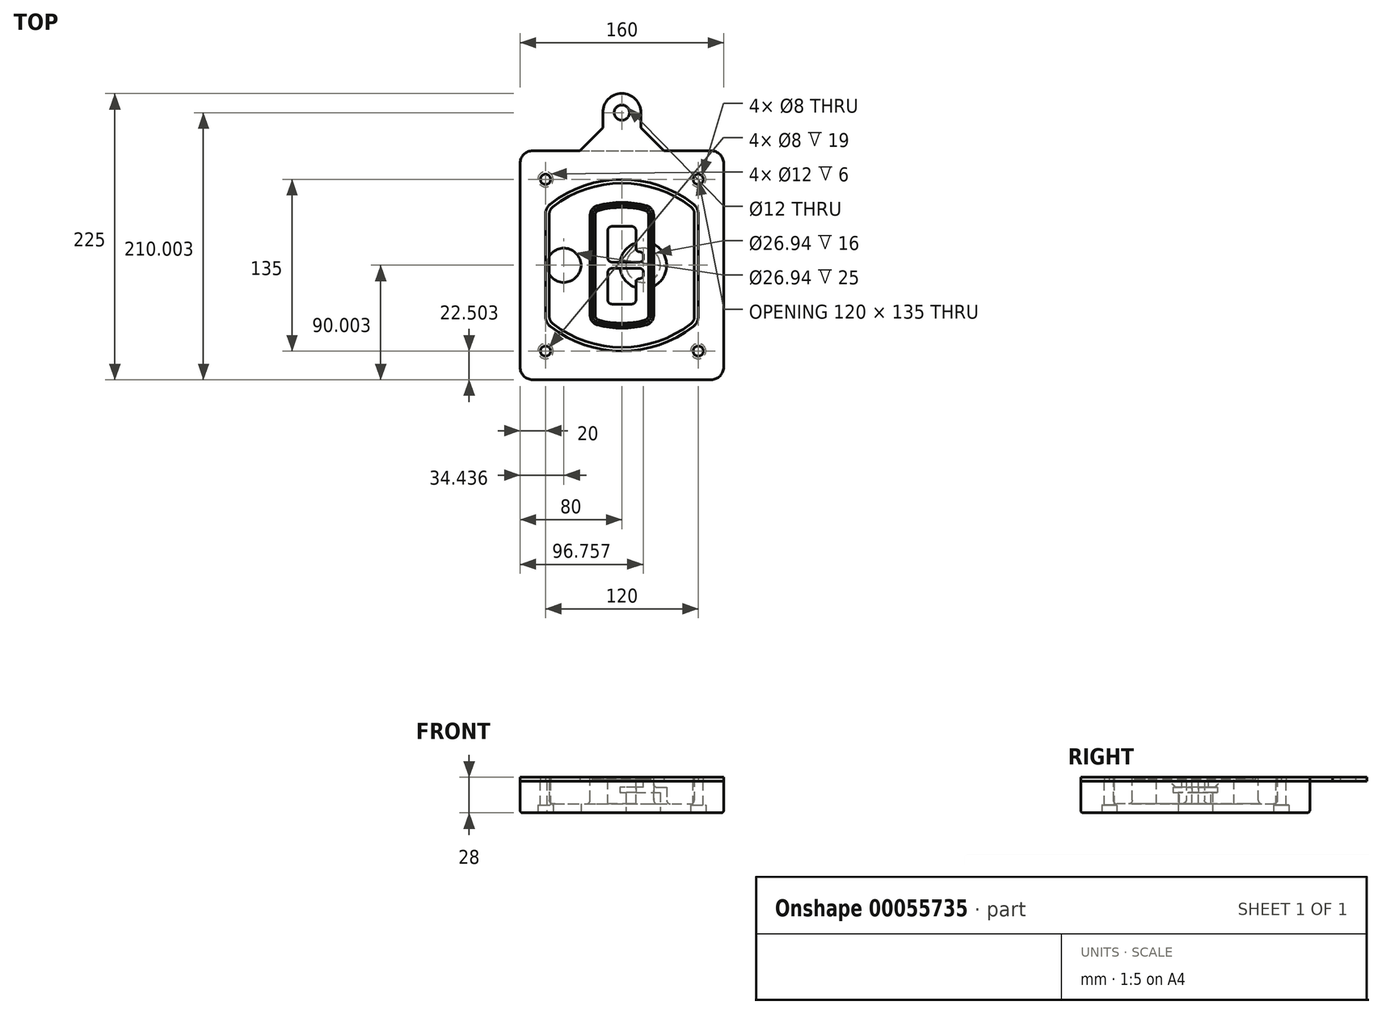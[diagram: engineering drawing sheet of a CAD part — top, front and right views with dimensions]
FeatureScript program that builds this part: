
annotation { "Feature Type Name" : "Feature", "Feature Type Description" : "" }
export const myFeature = defineFeature(function(context is Context, id is Id, definition is map)
    precondition{}
    {
        {
            var Q0;
            Q0=qCreatedBy(makeId("Top.planeOp"),FACE);
            var sketch = newSketch(context, id + "F0", { "sketchPlane" : qUnion([Q0])});
            skPoint(sketch, "E0.rect.middle", {"position": v(0, 0) * mm});
            skLineSegment(sketch, "E1.bottom", {"start": v(24.05, 28.38) * mm, "end": v(164.05, 28.38) * mm});
            skLineSegment(sketch, "E1.top", {"start": v(24.05, 208.38) * mm, "end": v(164.05, 208.38) * mm});
            skLineSegment(sketch, "E1.left", {"start": v(14.05, 38.38) * mm, "end": v(14.05, 198.38) * mm});
            skLineSegment(sketch, "E1.right", {"start": v(174.05, 38.38) * mm, "end": v(174.05, 198.38) * mm});
            skLineSegment(sketch, "E2", {"start": v(14.05, 208.38) * mm, "end": v(174.05, 28.38) * mm, "construction": true});
            skLineSegment(sketch, "E3", {"start": v(174.05, 208.38) * mm, "end": v(14.05, 28.38) * mm, "construction": true});
            skCircle(sketch, "E4", {"center": v(34.05, 185.88) * mm, "radius": 4 * mm});
            skCircle(sketch, "E5", {"center": v(154.05, 185.88) * mm, "radius": 4 * mm});
            skCircle(sketch, "E6", {"center": v(154.05, 50.88) * mm, "radius": 4 * mm});
            skCircle(sketch, "E7", {"center": v(34.05, 50.88) * mm, "radius": 4 * mm});
            skLineSegment(sketch, "E8", {"start": v(34.05, 185.88) * mm, "end": v(154.05, 185.88) * mm, "construction": true});
            skLineSegment(sketch, "E9", {"start": v(154.05, 185.88) * mm, "end": v(154.05, 50.88) * mm, "construction": true});
            skLineSegment(sketch, "E10", {"start": v(154.05, 50.88) * mm, "end": v(34.05, 50.88) * mm, "construction": true});
            skLineSegment(sketch, "E11", {"start": v(34.05, 50.88) * mm, "end": v(34.05, 185.88) * mm, "construction": true});
            skLineSegment(sketch, "E12", {"start": v(34.05, 158.68) * mm, "end": v(34.05, 78.09) * mm});
            skLineSegment(sketch, "E13", {"start": v(154.05, 158.68) * mm, "end": v(154.05, 78.09) * mm});
            skArc(sketch, "E14", {"start": v(150.2, 166.56) * mm, "mid": v(94.05, 185.88) * mm, "end": v(37.9, 166.56) * mm});
            skArc(sketch, "E15", {"start": v(37.9, 70.2) * mm, "mid": v(94.05, 50.88) * mm, "end": v(150.2, 70.2) * mm});
            skLineSegment(sketch, "E16", {"start": v(34.05, 118.38) * mm, "end": v(154.05, 118.38) * mm, "construction": true});
            skPoint(sketch, "E17.visualSharp", {"position": v(34.05, 73.38) * mm});
            skArc(sketch, "E17.filletArc", {"start": v(34.05, 78.09) * mm, "mid": v(35.06, 73.7) * mm, "end": v(37.9, 70.2) * mm});
            skPoint(sketch, "E18.visualSharp", {"position": v(34.05, 163.38) * mm});
            skArc(sketch, "E18.filletArc", {"start": v(37.9, 166.56) * mm, "mid": v(35.06, 163.06) * mm, "end": v(34.05, 158.68) * mm});
            skPoint(sketch, "E19.visualSharp", {"position": v(154.05, 163.38) * mm});
            skArc(sketch, "E19.filletArc", {"start": v(154.05, 158.68) * mm, "mid": v(153.04, 163.06) * mm, "end": v(150.2, 166.56) * mm});
            skPoint(sketch, "E20.visualSharp", {"position": v(154.05, 73.38) * mm});
            skArc(sketch, "E20.filletArc", {"start": v(150.2, 70.2) * mm, "mid": v(153.04, 73.7) * mm, "end": v(154.05, 78.09) * mm});
            skPoint(sketch, "E21.visualSharp", {"position": v(14.05, 208.38) * mm});
            skArc(sketch, "E21.filletArc", {"start": v(24.05, 208.38) * mm, "mid": v(16.98, 205.45) * mm, "end": v(14.05, 198.38) * mm});
            skPoint(sketch, "E22.visualSharp", {"position": v(174.05, 208.38) * mm});
            skArc(sketch, "E22.filletArc", {"start": v(174.05, 198.38) * mm, "mid": v(171.12, 205.45) * mm, "end": v(164.05, 208.38) * mm});
            skPoint(sketch, "E23.visualSharp", {"position": v(174.05, 28.38) * mm});
            skArc(sketch, "E23.filletArc", {"start": v(164.05, 28.38) * mm, "mid": v(171.12, 31.31) * mm, "end": v(174.05, 38.38) * mm});
            skPoint(sketch, "E24.visualSharp", {"position": v(14.05, 28.38) * mm});
            skArc(sketch, "E24.filletArc", {"start": v(14.05, 38.38) * mm, "mid": v(16.98, 31.31) * mm, "end": v(24.05, 28.38) * mm});
            skArc(sketch, "E25.0", {"start": v(151.05, 158.68) * mm, "mid": v(150.34, 161.75) * mm, "end": v(148.36, 164.2) * mm});
            skLineSegment(sketch, "E25.1", {"start": v(151.05, 158.68) * mm, "end": v(151.05, 78.09) * mm});
            skArc(sketch, "E25.2", {"start": v(148.36, 72.57) * mm, "mid": v(150.34, 75.02) * mm, "end": v(151.05, 78.09) * mm});
            skArc(sketch, "E25.3", {"start": v(39.74, 72.57) * mm, "mid": v(94.05, 53.88) * mm, "end": v(148.36, 72.57) * mm});
            skArc(sketch, "E25.4", {"start": v(37.05, 78.09) * mm, "mid": v(37.76, 75.02) * mm, "end": v(39.74, 72.57) * mm});
            skArc(sketch, "E25.5", {"start": v(148.36, 164.2) * mm, "mid": v(94.05, 182.88) * mm, "end": v(39.74, 164.2) * mm});
            skLineSegment(sketch, "E25.6", {"start": v(37.05, 158.68) * mm, "end": v(37.05, 78.09) * mm});
            skArc(sketch, "E25.7", {"start": v(39.74, 164.2) * mm, "mid": v(37.76, 161.75) * mm, "end": v(37.05, 158.68) * mm});
            skArc(sketch, "E26.0", {"start": v(35.43, 169.71) * mm, "mid": v(31.47, 164.82) * mm, "end": v(30.05, 158.68) * mm});
            skArc(sketch, "E26.1", {"start": v(152.67, 169.71) * mm, "mid": v(94.05, 189.88) * mm, "end": v(35.43, 169.71) * mm});
            skArc(sketch, "E26.2", {"start": v(158.05, 158.68) * mm, "mid": v(156.63, 164.82) * mm, "end": v(152.67, 169.71) * mm});
            skLineSegment(sketch, "E26.3", {"start": v(158.05, 158.68) * mm, "end": v(158.05, 78.09) * mm});
            skArc(sketch, "E26.4", {"start": v(152.67, 67.05) * mm, "mid": v(156.63, 71.95) * mm, "end": v(158.05, 78.09) * mm});
            skLineSegment(sketch, "E26.5", {"start": v(30.05, 158.68) * mm, "end": v(30.05, 78.09) * mm});
            skArc(sketch, "E26.6", {"start": v(35.43, 67.05) * mm, "mid": v(94.05, 46.88) * mm, "end": v(152.67, 67.05) * mm});
            skArc(sketch, "E26.7", {"start": v(30.05, 78.09) * mm, "mid": v(31.47, 71.95) * mm, "end": v(35.43, 67.05) * mm});
            skSolve(sketch);
        }
        {
            var Q0;
            Q0=makeQuery(id+"F0.imprint","IMPRINT",FACE,{"disambiguationData":[TD([[makeQuery(id+"F0.imprint","IMPRINT",EDGE,{"derivedFrom":sQuery(id+"F0.wireOp",EDGE,"E1.bottom")}),1.0]])]});
            var Q1;
            Q1=makeQuery(id+"F0.imprint","IMPRINT",FACE,{"disambiguationData":[TD([[makeQuery(id+"F0.imprint","IMPRINT",EDGE,{"derivedFrom":sQuery(id+"F0.wireOp",EDGE,"E12")}),1.0]])]});
            var Q2;
            Q2=makeQuery(id+"F0.imprint","IMPRINT",FACE,{"disambiguationData":[TD([[makeQuery(id+"F0.imprint","IMPRINT",EDGE,{"derivedFrom":sQuery(id+"F0.wireOp",EDGE,"E25.0")}),1.0]])]});
            var Q3;
            Q3=makeQuery(id+"F0.imprint","IMPRINT",FACE,{"disambiguationData":[TD([[makeQuery(id+"F0.imprint","IMPRINT",EDGE,{"derivedFrom":sQuery(id+"F0.wireOp",EDGE,"E12")}),-1.0]])]});
            extrude(context, id + "F1", {"entities" : qUnion([Q0, Q1, Q2, Q3]), "oppositeDirection" : true, "depth" : 25 * mm});
        }
        {
            var Q0;
            Q0=makeQuery(id+"F0.imprint","IMPRINT",FACE,{"disambiguationData":[TD([[makeQuery(id+"F0.imprint","IMPRINT",EDGE,{"derivedFrom":sQuery(id+"F0.wireOp",EDGE,"E12")}),1.0]])]});
            extrude(context, id + "F2", {"entities" : qUnion([Q0]), "operationType" : NewBodyOperationType.ADD, "depth" : 3 * mm});
        }
        {
            var Q0;
            Q0=makeQuery(id+"F0.imprint","IMPRINT",FACE,{"disambiguationData":[TD([[makeQuery(id+"F0.imprint","IMPRINT",EDGE,{"derivedFrom":sQuery(id+"F0.wireOp",EDGE,"E25.0")}),1.0]])]});
            extrude(context, id + "F3", {"entities" : qUnion([Q0]), "operationType" : NewBodyOperationType.REMOVE, "oppositeDirection" : true, "depth" : 18 * mm});
        }
        {
            var Q0;
            Q0=makeQuery(id+"F2.opExtrude","CAP_FACE",FACE,{"disambiguationData":[OSD([sQuery(id+"F0.wireOp",EDGE,"E12"),sQuery(id+"F0.wireOp",EDGE,"E13"),sQuery(id+"F0.wireOp",EDGE,"E14"),sQuery(id+"F0.wireOp",EDGE,"E15"),sQuery(id+"F0.wireOp",EDGE,"E17.filletArc"),sQuery(id+"F0.wireOp",EDGE,"E18.filletArc"),sQuery(id+"F0.wireOp",EDGE,"E19.filletArc"),sQuery(id+"F0.wireOp",EDGE,"E20.filletArc"),sQuery(id+"F0.wireOp",EDGE,"E25.0"),sQuery(id+"F0.wireOp",EDGE,"E25.1"),sQuery(id+"F0.wireOp",EDGE,"E25.2"),sQuery(id+"F0.wireOp",EDGE,"E25.3"),sQuery(id+"F0.wireOp",EDGE,"E25.4"),sQuery(id+"F0.wireOp",EDGE,"E25.5"),sQuery(id+"F0.wireOp",EDGE,"E25.6"),sQuery(id+"F0.wireOp",EDGE,"E25.7")])],"isStart":false});
            var sketch = newSketch(context, id + "F4", { "sketchPlane" : qUnion([Q0])});
            skArc(sketch, "E27.0", {"start": v(74.97, 71.41) * mm, "mid": v(94.05, 68.88) * mm, "end": v(113.13, 71.41) * mm});
            skArc(sketch, "E28.0", {"start": v(113.13, 165.35) * mm, "mid": v(94.05, 167.88) * mm, "end": v(74.97, 165.35) * mm});
            skLineSegment(sketch, "E29", {"start": v(69.05, 157.63) * mm, "end": v(69.05, 79.14) * mm});
            skLineSegment(sketch, "E30", {"start": v(119.05, 157.63) * mm, "end": v(119.05, 79.14) * mm});
            skLineSegment(sketch, "E31", {"start": v(69.05, 163.48) * mm, "end": v(119.05, 163.48) * mm, "construction": true});
            skLineSegment(sketch, "E32", {"start": v(69.05, 73.28) * mm, "end": v(119.05, 73.28) * mm, "construction": true});
            skPoint(sketch, "E33.visualSharp", {"position": v(69.05, 163.48) * mm});
            skArc(sketch, "E33.filletArc", {"start": v(74.97, 165.35) * mm, "mid": v(70.7, 162.5) * mm, "end": v(69.05, 157.63) * mm});
            skPoint(sketch, "E34.visualSharp", {"position": v(119.05, 163.48) * mm});
            skArc(sketch, "E34.filletArc", {"start": v(119.05, 157.63) * mm, "mid": v(117.4, 162.5) * mm, "end": v(113.13, 165.35) * mm});
            skPoint(sketch, "E35.visualSharp", {"position": v(119.05, 73.28) * mm});
            skArc(sketch, "E35.filletArc", {"start": v(113.13, 71.41) * mm, "mid": v(117.4, 74.27) * mm, "end": v(119.05, 79.14) * mm});
            skPoint(sketch, "E36.visualSharp", {"position": v(69.05, 73.28) * mm});
            skArc(sketch, "E36.filletArc", {"start": v(69.05, 79.14) * mm, "mid": v(70.7, 74.27) * mm, "end": v(74.97, 71.41) * mm});
            skArc(sketch, "E37.0", {"start": v(148.36, 164.2) * mm, "mid": v(94.05, 182.88) * mm, "end": v(39.74, 164.2) * mm});
            skArc(sketch, "E37.1", {"start": v(39.74, 164.2) * mm, "mid": v(37.76, 161.75) * mm, "end": v(37.05, 158.68) * mm});
            skLineSegment(sketch, "E37.2", {"start": v(37.05, 158.68) * mm, "end": v(37.05, 78.09) * mm});
            skArc(sketch, "E37.3", {"start": v(37.05, 78.09) * mm, "mid": v(37.76, 75.02) * mm, "end": v(39.74, 72.57) * mm});
            skArc(sketch, "E37.4", {"start": v(39.74, 72.57) * mm, "mid": v(94.05, 53.88) * mm, "end": v(148.36, 72.57) * mm});
            skArc(sketch, "E37.5", {"start": v(148.36, 72.57) * mm, "mid": v(150.34, 75.02) * mm, "end": v(151.05, 78.09) * mm});
            skLineSegment(sketch, "E37.6", {"start": v(151.05, 158.68) * mm, "end": v(151.05, 78.09) * mm});
            skArc(sketch, "E37.7", {"start": v(151.05, 158.68) * mm, "mid": v(150.34, 161.75) * mm, "end": v(148.36, 164.2) * mm});
            skLineSegment(sketch, "E38.0", {"start": v(117.05, 157.63) * mm, "end": v(117.05, 79.14) * mm});
            skArc(sketch, "E38.1", {"start": v(112.61, 73.34) * mm, "mid": v(115.81, 75.49) * mm, "end": v(117.05, 79.14) * mm});
            skArc(sketch, "E38.2", {"start": v(75.49, 73.34) * mm, "mid": v(94.05, 70.88) * mm, "end": v(112.61, 73.34) * mm});
            skArc(sketch, "E38.3", {"start": v(71.05, 79.14) * mm, "mid": v(72.29, 75.49) * mm, "end": v(75.49, 73.34) * mm});
            skLineSegment(sketch, "E38.4", {"start": v(71.05, 157.63) * mm, "end": v(71.05, 79.14) * mm});
            skArc(sketch, "E38.5", {"start": v(117.05, 157.63) * mm, "mid": v(115.81, 161.28) * mm, "end": v(112.61, 163.42) * mm});
            skArc(sketch, "E38.6", {"start": v(75.49, 163.42) * mm, "mid": v(72.29, 161.28) * mm, "end": v(71.05, 157.63) * mm});
            skArc(sketch, "E38.7", {"start": v(112.61, 163.42) * mm, "mid": v(94.05, 165.88) * mm, "end": v(75.49, 163.42) * mm});
            skArc(sketch, "E39.0", {"start": v(115.05, 157.63) * mm, "mid": v(114.23, 160.06) * mm, "end": v(112.1, 161.5) * mm});
            skLineSegment(sketch, "E39.1", {"start": v(115.05, 157.63) * mm, "end": v(115.05, 79.14) * mm});
            skArc(sketch, "E39.2", {"start": v(112.1, 75.27) * mm, "mid": v(114.23, 76.7) * mm, "end": v(115.05, 79.14) * mm});
            skArc(sketch, "E39.3", {"start": v(76, 75.27) * mm, "mid": v(94.05, 72.88) * mm, "end": v(112.1, 75.27) * mm});
            skArc(sketch, "E39.4", {"start": v(73.05, 79.14) * mm, "mid": v(73.87, 76.7) * mm, "end": v(76, 75.27) * mm});
            skArc(sketch, "E39.5", {"start": v(112.1, 161.5) * mm, "mid": v(94.05, 163.88) * mm, "end": v(76, 161.5) * mm});
            skLineSegment(sketch, "E39.6", {"start": v(73.05, 157.63) * mm, "end": v(73.05, 79.14) * mm});
            skArc(sketch, "E39.7", {"start": v(76, 161.5) * mm, "mid": v(73.87, 160.06) * mm, "end": v(73.05, 157.63) * mm});
            skLineSegment(sketch, "E40", {"start": v(69.05, 118.38) * mm, "end": v(119.05, 118.38) * mm, "construction": true});
            skLineSegment(sketch, "E41", {"start": v(83.05, 123.88) * mm, "end": v(83.05, 145.88) * mm});
            skLineSegment(sketch, "E42", {"start": v(86.05, 148.88) * mm, "end": v(102.05, 148.88) * mm});
            skLineSegment(sketch, "E43", {"start": v(105.05, 145.88) * mm, "end": v(105.05, 131.88) * mm});
            skLineSegment(sketch, "E44", {"start": v(108.05, 128.88) * mm, "end": v(108.05, 128.88) * mm});
            skLineSegment(sketch, "E45", {"start": v(111.05, 125.88) * mm, "end": v(111.05, 123.88) * mm});
            skLineSegment(sketch, "E46", {"start": v(108.05, 120.88) * mm, "end": v(86.05, 120.88) * mm});
            skPoint(sketch, "E47.visualSharp", {"position": v(83.05, 148.88) * mm});
            skArc(sketch, "E47.filletArc", {"start": v(86.05, 148.88) * mm, "mid": v(83.93, 148) * mm, "end": v(83.05, 145.88) * mm});
            skPoint(sketch, "E48.visualSharp", {"position": v(105.05, 148.88) * mm});
            skArc(sketch, "E48.filletArc", {"start": v(105.05, 145.88) * mm, "mid": v(104.17, 148) * mm, "end": v(102.05, 148.88) * mm});
            skPoint(sketch, "E49.visualSharp", {"position": v(105.05, 128.88) * mm});
            skArc(sketch, "E49.filletArc", {"start": v(105.05, 131.88) * mm, "mid": v(105.93, 129.76) * mm, "end": v(108.05, 128.88) * mm});
            skPoint(sketch, "E50.visualSharp", {"position": v(111.05, 128.88) * mm});
            skArc(sketch, "E50.filletArc", {"start": v(111.05, 125.88) * mm, "mid": v(110.17, 128) * mm, "end": v(108.05, 128.88) * mm});
            skPoint(sketch, "E51.visualSharp", {"position": v(111.05, 120.88) * mm});
            skArc(sketch, "E51.filletArc", {"start": v(108.05, 120.88) * mm, "mid": v(110.17, 121.76) * mm, "end": v(111.05, 123.88) * mm});
            skPoint(sketch, "E52.visualSharp", {"position": v(83.05, 120.88) * mm});
            skArc(sketch, "E52.filletArc", {"start": v(83.05, 123.88) * mm, "mid": v(83.93, 121.76) * mm, "end": v(86.05, 120.88) * mm});
            skLineSegment(sketch, "E53.0.MirrorCS", {"start": v(108.05, 115.88) * mm, "end": v(86.05, 115.88) * mm});
            skArc(sketch, "E54.0.MirrorCS", {"start": v(83.05, 112.88) * mm, "mid": v(83.93, 115) * mm, "end": v(86.05, 115.88) * mm});
            skLineSegment(sketch, "E55.0.MirrorCS", {"start": v(83.05, 112.88) * mm, "end": v(83.05, 90.88) * mm});
            skArc(sketch, "E56.0.MirrorCS", {"start": v(86.05, 87.88) * mm, "mid": v(83.93, 88.76) * mm, "end": v(83.05, 90.88) * mm});
            skLineSegment(sketch, "E57.0.MirrorCS", {"start": v(86.05, 87.88) * mm, "end": v(102.05, 87.88) * mm});
            skArc(sketch, "E58.0.MirrorCS", {"start": v(105.05, 90.88) * mm, "mid": v(104.17, 88.76) * mm, "end": v(102.05, 87.88) * mm});
            skLineSegment(sketch, "E59.0.MirrorCS", {"start": v(105.05, 90.88) * mm, "end": v(105.05, 104.88) * mm});
            skArc(sketch, "E60.0.MirrorCS", {"start": v(105.05, 104.88) * mm, "mid": v(105.93, 107) * mm, "end": v(108.05, 107.88) * mm});
            skArc(sketch, "E61.0.MirrorCS", {"start": v(111.05, 110.88) * mm, "mid": v(110.17, 108.76) * mm, "end": v(108.05, 107.88) * mm});
            skLineSegment(sketch, "E62.0.MirrorCS", {"start": v(111.05, 110.88) * mm, "end": v(111.05, 112.88) * mm});
            skArc(sketch, "E63.0.MirrorCS", {"start": v(108.05, 115.88) * mm, "mid": v(110.17, 115) * mm, "end": v(111.05, 112.88) * mm});
            skSolve(sketch);
        }
        {
            var Q0;
            Q0=makeQuery(id+"F4.imprint","IMPRINT",FACE,{"disambiguationData":[TD([[makeQuery(id+"F4.imprint","IMPRINT",EDGE,{"derivedFrom":sQuery(id+"F4.wireOp",EDGE,"E27.0")}),1.0]])]});
            var Q1;
            Q1=makeQuery(id+"F4.imprint","IMPRINT",FACE,{"disambiguationData":[TD([[makeQuery(id+"F4.imprint","IMPRINT",EDGE,{"derivedFrom":sQuery(id+"F4.wireOp",EDGE,"E38.0")}),-1.0]])]});
            var Q2;
            Q2=makeQuery(id+"F4.imprint","IMPRINT",FACE,{"disambiguationData":[TD([[makeQuery(id+"F4.imprint","IMPRINT",EDGE,{"derivedFrom":sQuery(id+"F4.wireOp",EDGE,"E39.0")}),1.0]])]});
            extrude(context, id + "F5", {"entities" : qUnion([Q0, Q1, Q2]), "operationType" : NewBodyOperationType.ADD, "endBound" : BoundingType.UP_TO_NEXT, "oppositeDirection" : true, "depth" : 25 * mm});
        }
        {
            var Q0;
            Q0=makeQuery(id+"F4.imprint","IMPRINT",FACE,{"disambiguationData":[TD([[makeQuery(id+"F4.imprint","IMPRINT",EDGE,{"derivedFrom":sQuery(id+"F4.wireOp",EDGE,"E38.0")}),-1.0]])]});
            extrude(context, id + "F6", {"entities" : qUnion([Q0]), "operationType" : NewBodyOperationType.REMOVE, "oppositeDirection" : true, "depth" : 2 * mm});
        }
        {
            var Q0;
            Q0=makeQuery(id+"F1.opExtrude","CAP_FACE",FACE,{"disambiguationData":[OSD([sQuery(id+"F0.wireOp",EDGE,"E1.bottom"),sQuery(id+"F0.wireOp",EDGE,"E1.top"),sQuery(id+"F0.wireOp",EDGE,"E1.left"),sQuery(id+"F0.wireOp",EDGE,"E1.right"),sQuery(id+"F0.wireOp",EDGE,"E4"),sQuery(id+"F0.wireOp",EDGE,"E5"),sQuery(id+"F0.wireOp",EDGE,"E6"),sQuery(id+"F0.wireOp",EDGE,"E7"),sQuery(id+"F0.wireOp",EDGE,"E21.filletArc"),sQuery(id+"F0.wireOp",EDGE,"E22.filletArc"),sQuery(id+"F0.wireOp",EDGE,"E23.filletArc"),sQuery(id+"F0.wireOp",EDGE,"E24.filletArc")])],"isStart":false});
            var sketch = newSketch(context, id + "F7", { "sketchPlane" : qUnion([Q0])});
            skCircle(sketch, "E64", {"center": v(110.8, -118.38) * mm, "radius": 13.47 * mm});
            skCircle(sketch, "E65", {"center": v(48.49, -118.38) * mm, "radius": 13.47 * mm});
            skLineSegment(sketch, "E66", {"start": v(174.05, -118.38) * mm, "end": v(14.05, -118.38) * mm});
            skCircle(sketch, "E67", {"center": v(110.8, -118.38) * mm, "radius": 18.47 * mm});
            skCircle(sketch, "E68", {"center": v(154.05, -185.88) * mm, "radius": 6 * mm});
            skCircle(sketch, "E69", {"center": v(34.05, -185.88) * mm, "radius": 6 * mm});
            skCircle(sketch, "E70", {"center": v(34.05, -50.88) * mm, "radius": 6 * mm});
            skCircle(sketch, "E71", {"center": v(154.05, -50.88) * mm, "radius": 6 * mm});
            skSolve(sketch);
        }
        {
            var Q0;
            {var subQ1=sQuery(id+"F7.wireOp",EDGE,"E66");var subQ4=sQuery(id+"F7.wireOp",EDGE,"E64");var subQ6=makeQuery(id+"F7.imprint","INTERSECT",VERTEX,{"disambiguationData":[OD(0.0)],"derivedFrom":[subQ4,subQ1]});Q0=makeQuery(id+"F7.imprint","IMPRINT",FACE,{"disambiguationData":[TD([[makeQuery(id+"F7.imprint","IMPRINT",EDGE,{"disambiguationData":[TD([[subQ6,-1.0]])],"derivedFrom":subQ4}),-1.0]])]});}
            var Q1;
            {var subQ0=sQuery(id+"F7.wireOp",EDGE,"E66");var subQ1=sQuery(id+"F7.wireOp",EDGE,"E64");var subQ3=makeQuery(id+"F7.imprint","INTERSECT",VERTEX,{"disambiguationData":[OD(0.0)],"derivedFrom":[subQ1,subQ0]});Q1=makeQuery(id+"F7.imprint","IMPRINT",FACE,{"disambiguationData":[TD([[makeQuery(id+"F7.imprint","IMPRINT",EDGE,{"disambiguationData":[TD([[subQ3,-1.0]])],"derivedFrom":subQ1}),1.0]])]});}
            var Q2;
            {var subQ0=sQuery(id+"F7.wireOp",EDGE,"E66");var subQ1=sQuery(id+"F7.wireOp",EDGE,"E64");var subQ3=makeQuery(id+"F7.imprint","INTERSECT",VERTEX,{"disambiguationData":[OD(0.0)],"derivedFrom":[subQ1,subQ0]});Q2=makeQuery(id+"F7.imprint","IMPRINT",FACE,{"disambiguationData":[TD([[makeQuery(id+"F7.imprint","IMPRINT",EDGE,{"disambiguationData":[TD([[subQ3,1.0]])],"derivedFrom":subQ1}),1.0]])]});}
            var Q3;
            {var subQ1=sQuery(id+"F7.wireOp",EDGE,"E66");var subQ4=sQuery(id+"F7.wireOp",EDGE,"E64");var subQ6=makeQuery(id+"F7.imprint","INTERSECT",VERTEX,{"disambiguationData":[OD(0.0)],"derivedFrom":[subQ4,subQ1]});Q3=makeQuery(id+"F7.imprint","IMPRINT",FACE,{"disambiguationData":[TD([[makeQuery(id+"F7.imprint","IMPRINT",EDGE,{"disambiguationData":[TD([[subQ6,1.0]])],"derivedFrom":subQ4}),-1.0]])]});}
            extrude(context, id + "F8", {"entities" : qUnion([Q0, Q1, Q2, Q3]), "operationType" : NewBodyOperationType.ADD, "oppositeDirection" : true, "depth" : 20 * mm});
        }
        {
            var Q0;
            {var subQ0=sQuery(id+"F7.wireOp",EDGE,"E66");var subQ1=sQuery(id+"F7.wireOp",EDGE,"E64");var subQ3=makeQuery(id+"F7.imprint","INTERSECT",VERTEX,{"disambiguationData":[OD(0.0)],"derivedFrom":[subQ1,subQ0]});Q0=makeQuery(id+"F7.imprint","IMPRINT",FACE,{"disambiguationData":[TD([[makeQuery(id+"F7.imprint","IMPRINT",EDGE,{"disambiguationData":[TD([[subQ3,-1.0]])],"derivedFrom":subQ1}),1.0]])]});}
            var Q1;
            {var subQ0=sQuery(id+"F7.wireOp",EDGE,"E66");var subQ1=sQuery(id+"F7.wireOp",EDGE,"E64");var subQ3=makeQuery(id+"F7.imprint","INTERSECT",VERTEX,{"disambiguationData":[OD(0.0)],"derivedFrom":[subQ1,subQ0]});Q1=makeQuery(id+"F7.imprint","IMPRINT",FACE,{"disambiguationData":[TD([[makeQuery(id+"F7.imprint","IMPRINT",EDGE,{"disambiguationData":[TD([[subQ3,1.0]])],"derivedFrom":subQ1}),1.0]])]});}
            extrude(context, id + "F9", {"entities" : qUnion([Q0, Q1]), "operationType" : NewBodyOperationType.REMOVE, "oppositeDirection" : true, "depth" : 16 * mm});
        }
        {
            var Q0;
            {var subQ0=sQuery(id+"F7.wireOp",EDGE,"E66");var subQ1=sQuery(id+"F7.wireOp",EDGE,"E65");var subQ3=makeQuery(id+"F7.imprint","INTERSECT",VERTEX,{"disambiguationData":[OD(0.0)],"derivedFrom":[subQ1,subQ0]});Q0=makeQuery(id+"F7.imprint","IMPRINT",FACE,{"disambiguationData":[TD([[makeQuery(id+"F7.imprint","IMPRINT",EDGE,{"disambiguationData":[TD([[subQ3,-1.0]])],"derivedFrom":subQ1}),1.0]])]});}
            var Q1;
            {var subQ0=sQuery(id+"F7.wireOp",EDGE,"E66");var subQ1=sQuery(id+"F7.wireOp",EDGE,"E65");var subQ3=makeQuery(id+"F7.imprint","INTERSECT",VERTEX,{"disambiguationData":[OD(0.0)],"derivedFrom":[subQ1,subQ0]});Q1=makeQuery(id+"F7.imprint","IMPRINT",FACE,{"disambiguationData":[TD([[makeQuery(id+"F7.imprint","IMPRINT",EDGE,{"disambiguationData":[TD([[subQ3,1.0]])],"derivedFrom":subQ1}),1.0]])]});}
            extrude(context, id + "F10", {"entities" : qUnion([Q0, Q1]), "operationType" : NewBodyOperationType.REMOVE, "oppositeDirection" : true, "depth" : 25 * mm});
        }
        {
            var Q0;
            Q0=makeQuery(id+"F7.imprint","IMPRINT",FACE,{"disambiguationData":[TD([[makeQuery(id+"F7.imprint","IMPRINT",EDGE,{"derivedFrom":sQuery(id+"F7.wireOp",EDGE,"E68")}),1.0]])]});
            var Q1;
            Q1=makeQuery(id+"F7.imprint","IMPRINT",FACE,{"disambiguationData":[TD([[makeQuery(id+"F7.imprint","IMPRINT",EDGE,{"derivedFrom":makeQuery(id+"F1.opExtrude","CAP_EDGE",EDGE,{"disambiguationData":[OSD([sQuery(id+"F0.wireOp",EDGE,"E5")])],"isStart":false})}),-1.0]])]});
            var Q2;
            Q2=makeQuery(id+"F7.imprint","IMPRINT",FACE,{"disambiguationData":[TD([[makeQuery(id+"F7.imprint","IMPRINT",EDGE,{"derivedFrom":sQuery(id+"F7.wireOp",EDGE,"E69")}),1.0]])]});
            var Q3;
            Q3=makeQuery(id+"F7.imprint","IMPRINT",FACE,{"disambiguationData":[TD([[makeQuery(id+"F7.imprint","IMPRINT",EDGE,{"derivedFrom":makeQuery(id+"F1.opExtrude","CAP_EDGE",EDGE,{"disambiguationData":[OSD([sQuery(id+"F0.wireOp",EDGE,"E4")])],"isStart":false})}),-1.0]])]});
            var Q4;
            Q4=makeQuery(id+"F7.imprint","IMPRINT",FACE,{"disambiguationData":[TD([[makeQuery(id+"F7.imprint","IMPRINT",EDGE,{"derivedFrom":sQuery(id+"F7.wireOp",EDGE,"E70")}),1.0]])]});
            var Q5;
            Q5=makeQuery(id+"F7.imprint","IMPRINT",FACE,{"disambiguationData":[TD([[makeQuery(id+"F7.imprint","IMPRINT",EDGE,{"derivedFrom":makeQuery(id+"F1.opExtrude","CAP_EDGE",EDGE,{"disambiguationData":[OSD([sQuery(id+"F0.wireOp",EDGE,"E7")])],"isStart":false})}),-1.0]])]});
            var Q6;
            Q6=makeQuery(id+"F7.imprint","IMPRINT",FACE,{"disambiguationData":[TD([[makeQuery(id+"F7.imprint","IMPRINT",EDGE,{"derivedFrom":sQuery(id+"F7.wireOp",EDGE,"E71")}),1.0]])]});
            var Q7;
            Q7=makeQuery(id+"F7.imprint","IMPRINT",FACE,{"disambiguationData":[TD([[makeQuery(id+"F7.imprint","IMPRINT",EDGE,{"derivedFrom":makeQuery(id+"F1.opExtrude","CAP_EDGE",EDGE,{"disambiguationData":[OSD([sQuery(id+"F0.wireOp",EDGE,"E6")])],"isStart":false})}),-1.0]])]});
            extrude(context, id + "F11", {"entities" : qUnion([Q0, Q1, Q2, Q3, Q4, Q5, Q6, Q7]), "operationType" : NewBodyOperationType.REMOVE, "oppositeDirection" : true, "depth" : 6 * mm});
        }
        {
            var Q0;
            Q0=makeQuery(id+"F9.boolean.opBoolean","COPY",FACE,{"derivedFrom":makeQuery(id+"F9.opExtrude","CAP_FACE",FACE,{"disambiguationData":[OSD([sQuery(id+"F7.wireOp",EDGE,"E64")])],"isStart":false})});
            var sketch = newSketch(context, id + "F12", { "sketchPlane" : qUnion([Q0])});
            skArc(sketch, "E72.0", {"start": v(105.05, -100.83) * mm, "mid": v(96.62, -106.56) * mm, "end": v(92.5, -115.88) * mm});
            skArc(sketch, "E72.1", {"start": v(92.5, -120.88) * mm, "mid": v(96.62, -130.2) * mm, "end": v(105.05, -135.93) * mm});
            skLineSegment(sketch, "E73", {"start": v(92.5, -120.88) * mm, "end": v(108.05, -120.88) * mm});
            skLineSegment(sketch, "E74.0", {"start": v(108.05, -115.88) * mm, "end": v(92.5, -115.88) * mm});
            skArc(sketch, "E74.1", {"start": v(108.05, -115.88) * mm, "mid": v(110.17, -115) * mm, "end": v(111.05, -112.88) * mm});
            skLineSegment(sketch, "E74.2", {"start": v(111.05, -110.88) * mm, "end": v(111.05, -112.88) * mm});
            skArc(sketch, "E74.3", {"start": v(111.05, -110.88) * mm, "mid": v(110.17, -108.76) * mm, "end": v(108.05, -107.88) * mm});
            skArc(sketch, "E74.4", {"start": v(105.05, -104.88) * mm, "mid": v(105.93, -107) * mm, "end": v(108.05, -107.88) * mm});
            skLineSegment(sketch, "E74.5", {"start": v(105.05, -100.83) * mm, "end": v(105.05, -104.88) * mm});
            skLineSegment(sketch, "E74.7", {"start": v(108.05, -120.88) * mm, "end": v(92.5, -120.88) * mm});
            skArc(sketch, "E74.8", {"start": v(108.05, -120.88) * mm, "mid": v(110.17, -121.76) * mm, "end": v(111.05, -123.88) * mm});
            skLineSegment(sketch, "E74.9", {"start": v(111.05, -125.88) * mm, "end": v(111.05, -123.88) * mm});
            skArc(sketch, "E74.10", {"start": v(111.05, -125.88) * mm, "mid": v(110.17, -128) * mm, "end": v(108.05, -128.88) * mm});
            skArc(sketch, "E74.11", {"start": v(105.05, -131.88) * mm, "mid": v(105.93, -129.76) * mm, "end": v(108.05, -128.88) * mm});
            skLineSegment(sketch, "E74.12", {"start": v(105.05, -135.93) * mm, "end": v(105.05, -131.88) * mm});
            skPoint(sketch, "E75.orphan", {"position": v(105.05, -145.88) * mm});
            skPoint(sketch, "E76.orphan", {"position": v(86.05, -120.88) * mm});
            skPoint(sketch, "E77.orphan", {"position": v(86.05, -115.88) * mm});
            skPoint(sketch, "E78.orphan", {"position": v(105.05, -90.88) * mm});
            skSolve(sketch);
        }
        {
            var Q0;
            {var subQ7=sQuery(id+"F12.wireOp",EDGE,"E72.0");var subQ14=sQuery(id+"F12.wireOp",EDGE,"E72.1");var subQ16=sQuery(id+"F12.wireOp",EDGE,"E74.1");var subQ18=sQuery(id+"F12.wireOp",EDGE,"E74.8");Q0=qUnion([makeQuery(id+"F12.imprint","IMPRINT",FACE,{"disambiguationData":[TD([[makeQuery(id+"F12.imprint","IMPRINT",EDGE,{"derivedFrom":subQ7}),1.0]])]}),makeQuery(id+"F12.imprint","IMPRINT",FACE,{"disambiguationData":[TD([[makeQuery(id+"F12.imprint","IMPRINT",EDGE,{"derivedFrom":subQ14}),1.0]])]}),makeQuery(id+"F12.imprint","IMPRINT",FACE,{"disambiguationData":[TD([[makeQuery(id+"F12.imprint","IMPRINT",EDGE,{"derivedFrom":subQ16}),1.0]])]}),makeQuery(id+"F12.imprint","IMPRINT",FACE,{"disambiguationData":[TD([[makeQuery(id+"F12.imprint","IMPRINT",EDGE,{"derivedFrom":subQ18}),-1.0]])]})]);}
            var Q1;
            Q1=makeQuery(id+"F5.boolean.opBoolean","SPLIT",FACE,{"disambiguationData":[TD([makeQuery(id+"F5.opExtrude","SWEPT_FACE",FACE,{"disambiguationData":[OSD([sQuery(id+"F4.wireOp",EDGE,"E41")])]})])],"derivedFrom":makeQuery(id+"F3.boolean.opBoolean","COPY",FACE,{"derivedFrom":makeQuery(id+"F3.opExtrude","CAP_FACE",FACE,{"disambiguationData":[OSD([sQuery(id+"F0.wireOp",EDGE,"E25.0"),sQuery(id+"F0.wireOp",EDGE,"E25.1"),sQuery(id+"F0.wireOp",EDGE,"E25.2"),sQuery(id+"F0.wireOp",EDGE,"E25.3"),sQuery(id+"F0.wireOp",EDGE,"E25.4"),sQuery(id+"F0.wireOp",EDGE,"E25.5"),sQuery(id+"F0.wireOp",EDGE,"E25.6"),sQuery(id+"F0.wireOp",EDGE,"E25.7")])],"isStart":false})})});
            extrude(context, id + "F13", {"entities" : qUnion([Q0]), "operationType" : NewBodyOperationType.REMOVE, "endBound" : BoundingType.UP_TO_SURFACE, "endBoundEntityFace" : qUnion([Q1]), "depth" : 25 * mm});
        }
        {
            var Q0;
            Q0=makeQuery(id+"F3.boolean.opBoolean","COPY",EDGE,{"derivedFrom":makeQuery(id+"F3.opExtrude","CAP_EDGE",EDGE,{"disambiguationData":[OSD([sQuery(id+"F0.wireOp",EDGE,"E25.6")])],"isStart":false})});
            var Q1;
            Q1=makeQuery(id+"F8.boolean.opBoolean","INTERSECT",EDGE,{"derivedFrom":[makeQuery(id+"F5.opExtrude","SWEPT_FACE",FACE,{"disambiguationData":[OSD([sQuery(id+"F4.wireOp",EDGE,"E30")])]}),makeQuery(id+"F8.opExtrude","CAP_FACE",FACE,{"disambiguationData":[OSD([sQuery(id+"F7.wireOp",EDGE,"E67")])],"isStart":false})]});
            var Q2;
            Q2=makeQuery(id+"F8.boolean.opBoolean","INTERSECT",EDGE,{"disambiguationData":[OD(1.0)],"derivedFrom":[makeQuery(id+"F5.opExtrude","SWEPT_FACE",FACE,{"disambiguationData":[OSD([sQuery(id+"F4.wireOp",EDGE,"E30")])]}),makeQuery(id+"F8.opExtrude","SWEPT_FACE",FACE,{"disambiguationData":[OSD([sQuery(id+"F7.wireOp",EDGE,"E67")])]})]});
            var Q3;
            {var subQ0=sQuery(id+"F4.wireOp",EDGE,"E30");Q3=makeQuery(id+"F8.boolean.opBoolean","SPLIT",EDGE,{"disambiguationData":[TD([makeQuery(id+"F5.opExtrude","SWEPT_FACE",FACE,{"disambiguationData":[OSD([sQuery(id+"F4.wireOp",EDGE,"E35.filletArc")])]})])],"derivedFrom":makeQuery(id+"F5.opExtrude","CAP_EDGE",EDGE,{"disambiguationData":[OSD([subQ0])],"isStart":false})});}
            var Q4;
            {var subQ0=sQuery(id+"F0.wireOp",EDGE,"E25.7");var subQ1=sQuery(id+"F0.wireOp",EDGE,"E25.1");var subQ2=sQuery(id+"F0.wireOp",EDGE,"E25.6");var subQ3=sQuery(id+"F0.wireOp",EDGE,"E25.5");var subQ4=sQuery(id+"F0.wireOp",EDGE,"E25.4");var subQ5=sQuery(id+"F0.wireOp",EDGE,"E25.0");var subQ6=sQuery(id+"F0.wireOp",EDGE,"E25.2");var subQ7=sQuery(id+"F0.wireOp",EDGE,"E25.3");Q4=makeQuery(id+"F8.boolean.opBoolean","INTERSECT",EDGE,{"derivedFrom":[makeQuery(id+"F5.boolean.opBoolean","SPLIT",FACE,{"disambiguationData":[TD([makeQuery(id+"F2.opExtrude","SWEPT_FACE",FACE,{"disambiguationData":[OSD([subQ5])]})])],"derivedFrom":makeQuery(id+"F3.boolean.opBoolean","COPY",FACE,{"derivedFrom":makeQuery(id+"F3.opExtrude","CAP_FACE",FACE,{"disambiguationData":[OSD([subQ5,subQ1,subQ6,subQ7,subQ4,subQ3,subQ2,subQ0])],"isStart":false})})}),makeQuery(id+"F8.opExtrude","SWEPT_FACE",FACE,{"disambiguationData":[OSD([sQuery(id+"F7.wireOp",EDGE,"E67")])]})]});}
            var Q5;
            Q5=makeQuery(id+"F8.boolean.opBoolean","INTERSECT",EDGE,{"disambiguationData":[OD(0.0)],"derivedFrom":[makeQuery(id+"F5.opExtrude","SWEPT_FACE",FACE,{"disambiguationData":[OSD([sQuery(id+"F4.wireOp",EDGE,"E30")])]}),makeQuery(id+"F8.opExtrude","SWEPT_FACE",FACE,{"disambiguationData":[OSD([sQuery(id+"F7.wireOp",EDGE,"E67")])]})]});
            fillet(context, id + "F14", {"entities" : qUnion([Q0, Q1, Q2, Q3, Q4, Q5]), "radius" : 3 * mm, "tangentPropagation" : true, "allowEdgeOverflow" : false});
        }
        {
            var Q0;
            Q0=makeQuery(id+"F1.opExtrude","CAP_EDGE",EDGE,{"disambiguationData":[OSD([sQuery(id+"F0.wireOp",EDGE,"E1.bottom")])],"isStart":false});
            fillet(context, id + "F15", {"entities" : qUnion([Q0]), "radius" : 2 * mm, "tangentPropagation" : true, "allowEdgeOverflow" : false});
        }
        {
            var Q0;
            {var subQ0=sQuery(id+"F0.wireOp",EDGE,"E22.filletArc");var subQ1=sQuery(id+"F0.wireOp",EDGE,"E7");var subQ2=sQuery(id+"F0.wireOp",EDGE,"E6");var subQ3=sQuery(id+"F0.wireOp",EDGE,"E5");var subQ4=sQuery(id+"F0.wireOp",EDGE,"E4");var subQ5=sQuery(id+"F0.wireOp",EDGE,"E1.bottom");var subQ6=sQuery(id+"F0.wireOp",EDGE,"E21.filletArc");var subQ7=sQuery(id+"F0.wireOp",EDGE,"E1.top");var subQ8=sQuery(id+"F0.wireOp",EDGE,"E1.left");var subQ9=sQuery(id+"F0.wireOp",EDGE,"E1.right");var subQ10=sQuery(id+"F0.wireOp",EDGE,"E23.filletArc");var subQ11=sQuery(id+"F0.wireOp",EDGE,"E24.filletArc");Q0=makeQuery(id+"F2.boolean.opBoolean","SPLIT",FACE,{"disambiguationData":[TD([makeQuery(id+"F1.opExtrude","SWEPT_FACE",FACE,{"disambiguationData":[OSD([subQ5])]})])],"derivedFrom":makeQuery(id+"F1.opExtrude","CAP_FACE",FACE,{"disambiguationData":[OSD([subQ5,subQ7,subQ8,subQ9,subQ4,subQ3,subQ2,subQ1,subQ6,subQ0,subQ10,subQ11])],"isStart":true})});}
            var sketch = newSketch(context, id + "F16", { "sketchPlane" : qUnion([Q0])});
            skLineSegment(sketch, "E79", {"start": v(94.05, 208.38) * mm, "end": v(94.05, 238.38) * mm, "construction": true});
            skCircle(sketch, "E80", {"center": v(94.05, 238.38) * mm, "radius": 6 * mm});
            skArc(sketch, "E81", {"start": v(109.05, 238.38) * mm, "mid": v(94.05, 253.38) * mm, "end": v(79.05, 238.38) * mm});
            skLineSegment(sketch, "E82", {"start": v(109.05, 238.38) * mm, "end": v(109.05, 226.38) * mm});
            skLineSegment(sketch, "E83", {"start": v(109.05, 226.38) * mm, "end": v(127.05, 208.38) * mm});
            skLineSegment(sketch, "E84", {"start": v(79.05, 238.38) * mm, "end": v(79.05, 226.38) * mm});
            skLineSegment(sketch, "E85", {"start": v(79.05, 226.38) * mm, "end": v(61.05, 208.38) * mm});
            skLineSegment(sketch, "E86", {"start": v(14.05, 118.38) * mm, "end": v(174.05, 118.38) * mm, "construction": true});
            skArc(sketch, "E87.MirrorCS", {"start": v(109.05, -1.62) * mm, "mid": v(94.05, -16.62) * mm, "end": v(79.05, -1.62) * mm});
            skCircle(sketch, "E88.MirrorC", {"center": v(94.05, -1.62) * mm, "radius": 6 * mm});
            skLineSegment(sketch, "E89.MirrorCS", {"start": v(109.05, -1.62) * mm, "end": v(109.05, 10.38) * mm});
            skLineSegment(sketch, "E90.MirrorCS", {"start": v(79.05, -1.62) * mm, "end": v(79.05, 10.38) * mm});
            skLineSegment(sketch, "E91.MirrorCS", {"start": v(94.05, 28.38) * mm, "end": v(94.05, -1.62) * mm, "construction": true});
            skLineSegment(sketch, "E92.MirrorCS", {"start": v(79.05, 10.38) * mm, "end": v(61.05, 28.38) * mm});
            skLineSegment(sketch, "E93.MirrorCS", {"start": v(109.05, 10.38) * mm, "end": v(127.05, 28.38) * mm});
            skSolve(sketch);
        }
        {
            var Q0;
            Q0=makeQuery(id+"F16.imprint","IMPRINT",FACE,{"disambiguationData":[TD([[makeQuery(id+"F16.imprint","IMPRINT",EDGE,{"derivedFrom":sQuery(id+"F16.wireOp",EDGE,"E80")}),-1.0]])]});
            var Q1;
            Q1=makeQuery(id+"F16.imprint","IMPRINT",FACE,{"disambiguationData":[TD([[makeQuery(id+"F16.imprint","IMPRINT",EDGE,{"derivedFrom":makeQuery(id+"F1.opExtrude","CAP_EDGE",EDGE,{"disambiguationData":[OSD([sQuery(id+"F0.wireOp",EDGE,"E1.left")])],"isStart":true})}),-1.0]])]});
            var Q2;
            Q2=makeQuery(id+"F16.imprint","IMPRINT",FACE,{"disambiguationData":[TD([[makeQuery(id+"F16.imprint","IMPRINT",EDGE,{"derivedFrom":sQuery(id+"F16.wireOp",EDGE,"E87.MirrorCS")}),-1.0]])]});
            var Q3;
            Q3=makeQuery(id+"F2.opExtrude","CAP_FACE",FACE,{"disambiguationData":[OSD([sQuery(id+"F0.wireOp",EDGE,"E12"),sQuery(id+"F0.wireOp",EDGE,"E13"),sQuery(id+"F0.wireOp",EDGE,"E14"),sQuery(id+"F0.wireOp",EDGE,"E15"),sQuery(id+"F0.wireOp",EDGE,"E17.filletArc"),sQuery(id+"F0.wireOp",EDGE,"E18.filletArc"),sQuery(id+"F0.wireOp",EDGE,"E19.filletArc"),sQuery(id+"F0.wireOp",EDGE,"E20.filletArc"),sQuery(id+"F0.wireOp",EDGE,"E25.0"),sQuery(id+"F0.wireOp",EDGE,"E25.1"),sQuery(id+"F0.wireOp",EDGE,"E25.2"),sQuery(id+"F0.wireOp",EDGE,"E25.3"),sQuery(id+"F0.wireOp",EDGE,"E25.4"),sQuery(id+"F0.wireOp",EDGE,"E25.5"),sQuery(id+"F0.wireOp",EDGE,"E25.6"),sQuery(id+"F0.wireOp",EDGE,"E25.7")])],"isStart":false});
            extrude(context, id + "F17", {"entities" : qUnion([Q0, Q1, Q2]), "endBound" : BoundingType.UP_TO_SURFACE, "endBoundEntityFace" : qUnion([Q3]), "depth" : 25.4 * mm});
        }
    });
